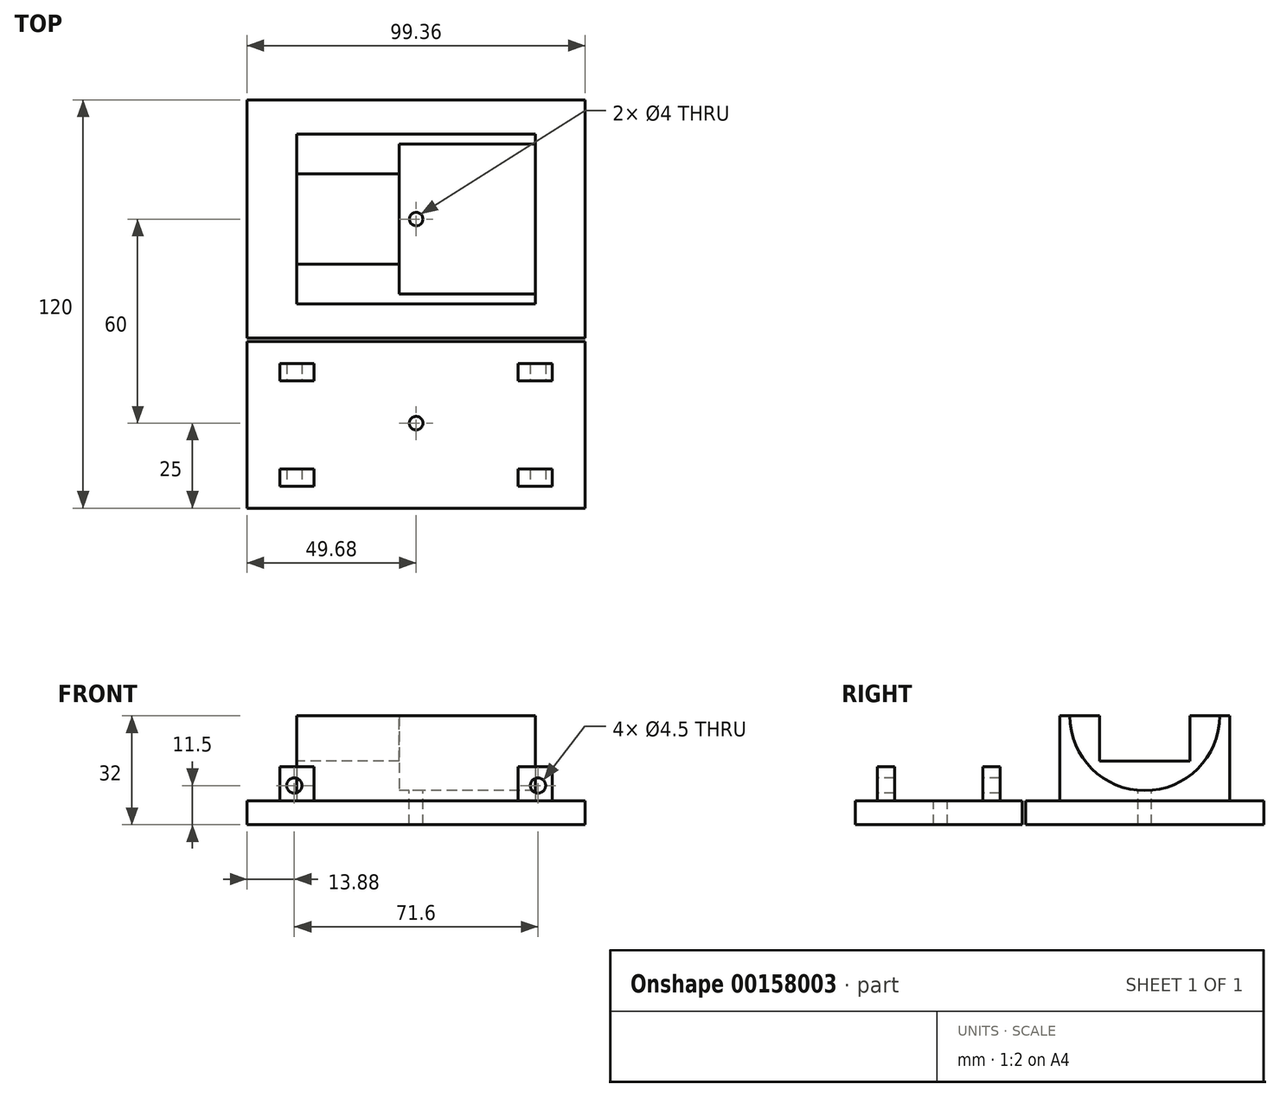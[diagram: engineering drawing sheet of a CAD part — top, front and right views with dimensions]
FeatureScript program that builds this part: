
annotation { "Feature Type Name" : "Feature", "Feature Type Description" : "" }
export const myFeature = defineFeature(function(context is Context, id is Id, definition is map)
    precondition{}
    {
        {
            var Q0;
            Q0=qCreatedBy(makeId("Top.planeOp"),FACE);
            var sketch = newSketch(context, id + "F0", { "sketchPlane" : qUnion([Q0])});
            skLineSegment(sketch, "E0.bottom", {"start": v(49.68, -60) * mm, "end": v(-49.68, -60) * mm});
            skLineSegment(sketch, "E0.top", {"start": v(49.68, 60) * mm, "end": v(-49.68, 60) * mm});
            skLineSegment(sketch, "E0.left", {"start": v(49.68, -60) * mm, "end": v(49.68, 60) * mm});
            skLineSegment(sketch, "E0.right", {"start": v(-49.68, -60) * mm, "end": v(-49.68, 60) * mm});
            skCircle(sketch, "E1", {"center": v(0, 25) * mm, "radius": 2 * mm});
            skCircle(sketch, "E2", {"center": v(0, -35) * mm, "radius": 2 * mm});
            skSolve(sketch);
        }
        {
            var Q0;
            Q0 = qSketchRegion(id + "F0", true);
            extrude(context, id + "F1", {"entities" : qUnion([Q0]), "oppositeDirection" : true, "depth" : 7 * mm});
        }
        {
            var Q0;
            Q0=makeQuery(id+"F1.opExtrude","CAP_FACE",FACE,{"disambiguationData":[OSD([sQuery(id+"F0.wireOp",EDGE,"E0.bottom"),sQuery(id+"F0.wireOp",EDGE,"E0.top"),sQuery(id+"F0.wireOp",EDGE,"E0.left"),sQuery(id+"F0.wireOp",EDGE,"E0.right"),sQuery(id+"F0.wireOp",EDGE,"AJBnLrOl-uYij-117d-noxO-RAuNQtY9KvCR")])],"isStart":true});
            var sketch = newSketch(context, id + "F2", { "sketchPlane" : qUnion([Q0])});
            skLineSegment(sketch, "E3.bottom", {"start": v(35, 0) * mm, "end": v(-35, 0) * mm});
            skLineSegment(sketch, "E3.top", {"start": v(35, 50) * mm, "end": v(-35, 50) * mm});
            skLineSegment(sketch, "E3.left", {"start": v(35, 0) * mm, "end": v(35, 50) * mm});
            skLineSegment(sketch, "E3.right", {"start": v(-35, 0) * mm, "end": v(-35, 50) * mm});
            skPoint(sketch, "E3.middle", {"position": v(0, 25) * mm});
            skLineSegment(sketch, "E4.bottom", {"start": v(40, -22.5) * mm, "end": v(-40, -22.5) * mm});
            skLineSegment(sketch, "E4.top", {"start": v(40, -17.5) * mm, "end": v(30, -17.5) * mm});
            skLineSegment(sketch, "E4.left", {"start": v(40, -22.5) * mm, "end": v(40, -17.5) * mm});
            skLineSegment(sketch, "E4.right", {"start": v(-40, -22.5) * mm, "end": v(-40, -17.5) * mm});
            skPoint(sketch, "E4.middle", {"position": v(0, -20) * mm});
            skLineSegment(sketch, "E5.bottom", {"start": v(40, -53.5) * mm, "end": v(30, -53.5) * mm});
            skLineSegment(sketch, "E5.top", {"start": v(40, -48.5) * mm, "end": v(-40, -48.5) * mm});
            skLineSegment(sketch, "E5.left", {"start": v(40, -53.5) * mm, "end": v(40, -48.5) * mm});
            skLineSegment(sketch, "E5.right", {"start": v(-40, -53.5) * mm, "end": v(-40, -48.5) * mm});
            skPoint(sketch, "E5.middle", {"position": v(0, -51) * mm});
            skLineSegment(sketch, "E6", {"start": v(30, -17.5) * mm, "end": v(30, -53.5) * mm});
            skLineSegment(sketch, "E7.MirrorCS", {"start": v(-30, -17.5) * mm, "end": v(-30, -53.5) * mm});
            skLineSegment(sketch, "E8.trimOffspring", {"start": v(-30, -17.5) * mm, "end": v(-40, -17.5) * mm});
            skLineSegment(sketch, "E9.trimOffspring", {"start": v(-30, -53.5) * mm, "end": v(-40, -53.5) * mm});
            skSolve(sketch);
        }
        {
            var Q0;
            Q0=makeQuery(id+"F2.imprint","IMPRINT",FACE,{"disambiguationData":[TD([[makeQuery(id+"F2.imprint","IMPRINT",EDGE,{"derivedFrom":makeQuery(id+"F1.opExtrude","CAP_EDGE",EDGE,{"disambiguationData":[OSD([sQuery(id+"F0.wireOp",EDGE,"AJBnLrOl-uYij-117d-noxO-RAuNQtY9KvCR")])],"isStart":true})}),1.0]])]});
            var Q1;
            Q1=makeQuery(id+"F2.imprint","IMPRINT",FACE,{"disambiguationData":[TD([[makeQuery(id+"F2.imprint","IMPRINT",EDGE,{"derivedFrom":sQuery(id+"F2.wireOp",EDGE,"E3.top")}),1.0]])]});
            var Q2;
            {var subQ0=sQuery(id+"F2.wireOp",EDGE,"E3.bottom");var subQ1=makeQuery(id+"F1.opExtrude","CAP_EDGE",EDGE,{"disambiguationData":[OSD([sQuery(id+"F0.wireOp",EDGE,"ZjPK8XqK-bpHb-ZdKa-9Ad8-f3XSbR7K4PLZ")])],"isStart":true});var subQ2=makeQuery(id+"F2.imprint","INTERSECT",VERTEX,{"disambiguationData":[OD(0.0)],"derivedFrom":[subQ1,subQ0]});Q2=makeQuery(id+"F2.imprint","IMPRINT",FACE,{"disambiguationData":[TD([[makeQuery(id+"F2.imprint","IMPRINT",EDGE,{"disambiguationData":[TD([[subQ2,-1.0]])],"derivedFrom":subQ0}),-1.0]])]});}
            extrude(context, id + "F3", {"entities" : qUnion([Q0, Q1, Q2]), "operationType" : NewBodyOperationType.ADD, "depth" : 25 * mm});
        }
        {
            var Q0;
            Q0=makeQuery(id+"F2.imprint","IMPRINT",FACE,{"disambiguationData":[TD([[makeQuery(id+"F2.imprint","IMPRINT",EDGE,{"derivedFrom":sQuery(id+"F2.wireOp",EDGE,"E3.bottom")}),-1.0]])]});
            var Q1;
            {var subQ0=sQuery(id+"F2.wireOp",EDGE,"E4.right");Q1=makeQuery(id+"F2.imprint","IMPRINT",FACE,{"disambiguationData":[TD([[makeQuery(id+"F2.imprint","IMPRINT",EDGE,{"derivedFrom":subQ0}),-1.0]])]});}
            var Q2;
            {var subQ0=sQuery(id+"F2.wireOp",EDGE,"E5.bottom");Q2=makeQuery(id+"F2.imprint","IMPRINT",FACE,{"disambiguationData":[TD([[makeQuery(id+"F2.imprint","IMPRINT",EDGE,{"derivedFrom":subQ0}),-1.0]])]});}
            var Q3;
            {var subQ0=sQuery(id+"F2.wireOp",EDGE,"E5.right");Q3=makeQuery(id+"F2.imprint","IMPRINT",FACE,{"disambiguationData":[TD([[makeQuery(id+"F2.imprint","IMPRINT",EDGE,{"derivedFrom":subQ0}),-1.0]])]});}
            var Q4;
            {var subQ4=sQuery(id+"F2.wireOp",EDGE,"E4.top");Q4=makeQuery(id+"F2.imprint","IMPRINT",FACE,{"disambiguationData":[TD([[makeQuery(id+"F2.imprint","IMPRINT",EDGE,{"derivedFrom":subQ4}),1.0]])]});}
            extrude(context, id + "F4", {"entities" : qUnion([Q0, Q1, Q2, Q3, Q4]), "operationType" : NewBodyOperationType.ADD, "depth" : 10 * mm});
        }
        {
            var Q0;
            Q0=qCreatedBy(makeId("Right.planeOp"),FACE);
            var sketch = newSketch(context, id + "F5", { "sketchPlane" : qUnion([Q0])});
            skCircle(sketch, "E10", {"center": v(25, 25) * mm, "radius": 22 * mm});
            skSolve(sketch);
        }
        {
            var Q0;
            Q0 = qSketchRegion(id + "F5", true);
            extrude(context, id + "F6", {"entities" : qUnion([Q0]), "operationType" : NewBodyOperationType.REMOVE, "depth" : 35 * mm, "hasSecondDirection" : true, "secondDirectionOppositeDirection" : true, "secondDirectionDepth" : 5 * mm});
        }
        {
            var Q0;
            Q0=makeQuery(id+"F3.opExtrude","SWEPT_FACE",FACE,{"disambiguationData":[OSD([sQuery(id+"F2.wireOp",EDGE,"E3.right")])]});
            var sketch = newSketch(context, id + "F7", { "sketchPlane" : qUnion([Q0])});
            skLineSegment(sketch, "E11.bottom", {"start": v(-11.75, 11.75) * mm, "end": v(-38.25, 11.75) * mm});
            skLineSegment(sketch, "E11.top", {"start": v(-11.75, 38.25) * mm, "end": v(-38.25, 38.25) * mm});
            skLineSegment(sketch, "E11.left", {"start": v(-11.75, 11.75) * mm, "end": v(-11.75, 38.25) * mm});
            skLineSegment(sketch, "E11.right", {"start": v(-38.25, 11.75) * mm, "end": v(-38.25, 38.25) * mm});
            skPoint(sketch, "E11.middle", {"position": v(-25, 25) * mm});
            skSolve(sketch);
        }
        {
            var Q0;
            Q0 = qSketchRegion(id + "F7", true);
            extrude(context, id + "F8", {"entities" : qUnion([Q0]), "operationType" : NewBodyOperationType.REMOVE, "oppositeDirection" : true, "depth" : 30 * mm});
        }
        {
            var Q0;
            Q0=makeQuery(id+"F4.opExtrude","SWEPT_FACE",FACE,{"disambiguationData":[OSD([sQuery(id+"F2.wireOp",EDGE,"E5.bottom")])]});
            var sketch = newSketch(context, id + "F9", { "sketchPlane" : qUnion([Q0])});
            skCircle(sketch, "E12", {"center": v(35.8, 4.5) * mm, "radius": 2.25 * mm});
            skCircle(sketch, "E13.MirrorC", {"center": v(-35.8, 4.5) * mm, "radius": 2.25 * mm});
            skSolve(sketch);
        }
        {
            var Q0;
            Q0 = qSketchRegion(id + "F9", true);
            extrude(context, id + "F10", {"entities" : qUnion([Q0]), "operationType" : NewBodyOperationType.REMOVE, "oppositeDirection" : true, "depth" : 40 * mm});
        }
        {
            var Q0;
            Q0=makeQuery(id+"F1.opExtrude","CAP_FACE",FACE,{"disambiguationData":[OSD([sQuery(id+"F0.wireOp",EDGE,"E0.bottom"),sQuery(id+"F0.wireOp",EDGE,"E0.top"),sQuery(id+"F0.wireOp",EDGE,"E0.left"),sQuery(id+"F0.wireOp",EDGE,"E0.right"),sQuery(id+"F0.wireOp",EDGE,"ZjPK8XqK-bpHb-ZdKa-9Ad8-f3XSbR7K4PLZ")])],"isStart":false});
            var sketch = newSketch(context, id + "F11", { "sketchPlane" : qUnion([Q0])});
            skLineSegment(sketch, "E14.bottom", {"start": v(49.68, 10) * mm, "end": v(-49.68, 10) * mm});
            skLineSegment(sketch, "E14.top", {"start": v(49.68, 11) * mm, "end": v(-49.68, 11) * mm});
            skLineSegment(sketch, "E14.left", {"start": v(49.68, 10) * mm, "end": v(49.68, 11) * mm});
            skLineSegment(sketch, "E14.right", {"start": v(-49.68, 10) * mm, "end": v(-49.68, 11) * mm});
            skSolve(sketch);
        }
        {
            var Q0;
            Q0 = qSketchRegion(id + "F11", true);
            extrude(context, id + "F12", {"entities" : qUnion([Q0]), "operationType" : NewBodyOperationType.REMOVE, "oppositeDirection" : true, "depth" : 25 * mm});
        }
    });
